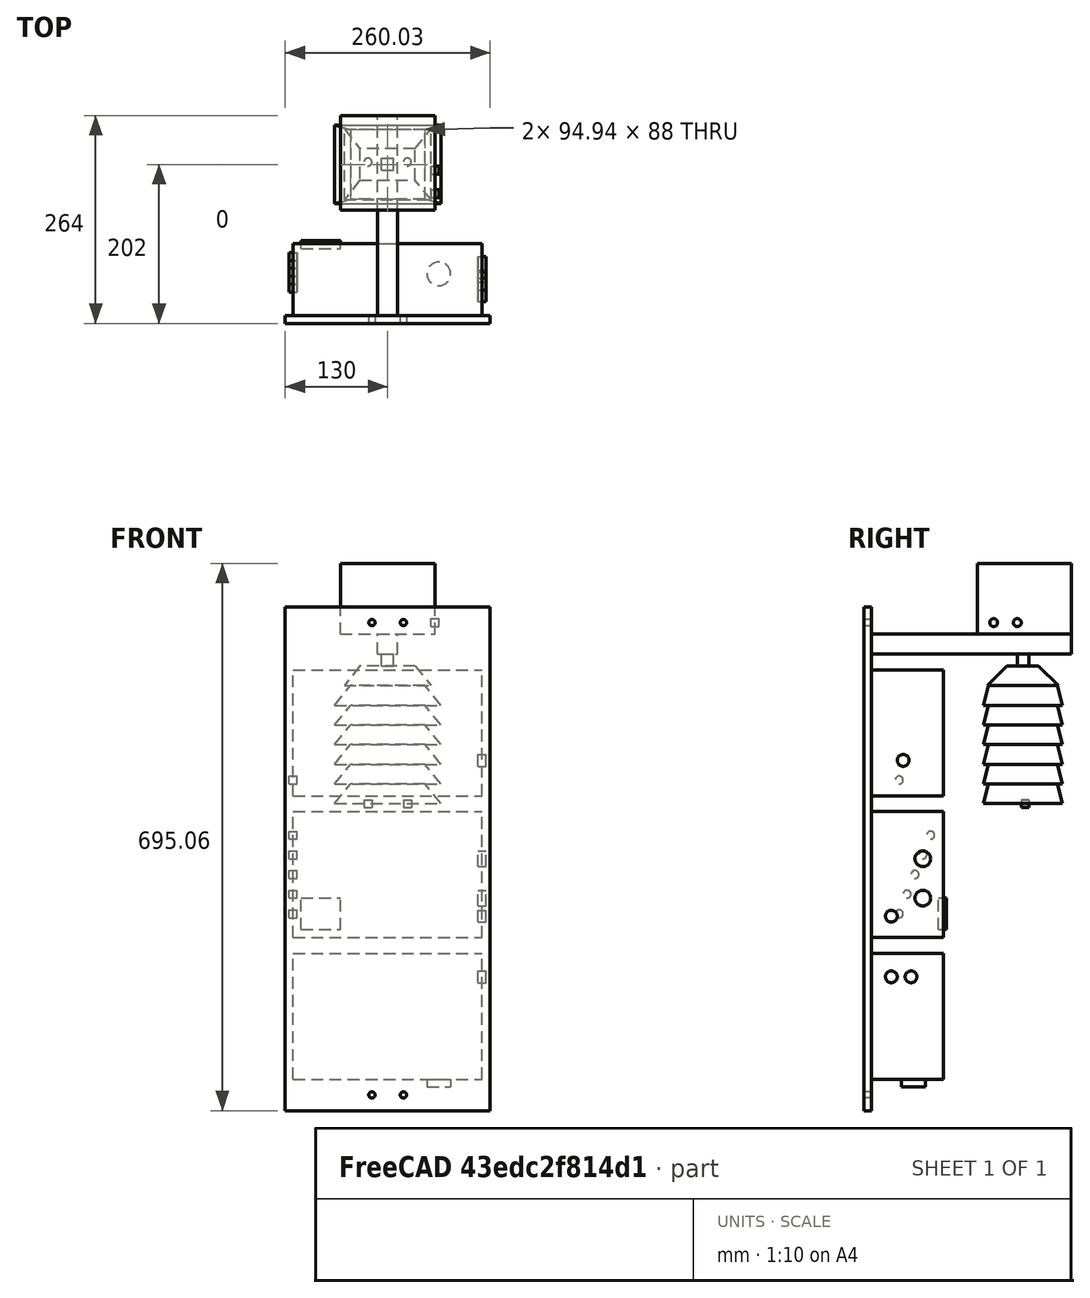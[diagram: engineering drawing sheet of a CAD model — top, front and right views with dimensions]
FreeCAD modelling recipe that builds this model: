
FCSTD DOCUMENT  (FreeCAD 0.17R13541 (Git))
Label: centralNode2019
License: All rights reserved
LicenseURL: http://en.wikipedia.org/wiki/All_rights_reserved
objects: Part::Box×38, Part::Cylinder×19, Part::Cut×17, Part::MultiCommon×10, Part::MultiFuse×3
note: 87 computed .brp shape members not serialized (recipe doc carries the construction recipe); baked Part::Feature solids carry a one-line shape summary decoded from their .brp

FEATURE [Part::Box] Box  label="Power Module "
  AttacherType = Attacher::AttachEngine3D
  Height = 160.02
  Length = 240.03
  Width = 91.44
FEATURE [Part::Box] Box001  label="Main Module"
  AttacherType = Attacher::AttachEngine3D
  Height = 160.02
  Length = 240.03
  Placement = pos=(0,0,180) rot=(0,0,1;0rad)
  Width = 91.44
FEATURE [Part::Box] Box002  label="Ozone Module"
  AttacherType = Attacher::AttachEngine3D
  Height = 160.02
  Length = 240.03
  Placement = pos=(0,0,360) rot=(0,0,1;0rad)
  Width = 91.44
FEATURE [Part::Box] Box003  label="Light Module"
  AttacherType = Attacher::AttachEngine3D
  Height = 89.66
  Length = 119.89
  Placement = pos=(60.05,134.1,565.4) rot=(0,0,1;0rad)
  Width = 119.89
FEATURE [Part::Box] Box005  label="Railing"
  AttacherType = Attacher::AttachEngine3D
  Height = 25.4
  Length = 25.4
  Placement = pos=(107.3,0,540) rot=(0,0,1;0rad)
  Width = 254
FEATURE [Part::Box] Box006  label="BackPanel"
  AttacherType = Attacher::AttachEngine3D
  Height = 640
  Length = 260.03
  Placement = pos=(-10,-10,-40) rot=(0,0,1;0rad)
  Width = 10
FEATURE [Part::Box] Box008  label="Cube001"
  AttacherType = Attacher::AttachEngine3D
  Height = 200
  Length = 200
  Placement = pos=(-22,-226,0) rot=(-1,0,0;0.235619rad)
  Width = 500
FEATURE [Part::Box] Box009  label="Acu1"
  AttacherType = Attacher::AttachEngine3D
  Height = 25
  Length = 135
  Placement = pos=(0,-226,0) rot=(0,0,1;0rad)
  Width = 100
FEATURE [Part::Box] Box010  label="Cube"
  AttacherType = Attacher::AttachEngine3D
  Height = 200
  Length = 20
  Placement = pos=(135,-236,0) rot=(0,-1,0;0.675442rad)
  Width = 500
FEATURE [Part::Box] Box011  label="Cube002"
  AttacherType = Attacher::AttachEngine3D
  Height = 500
  Length = 500
  Placement = pos=(0,-236,0) rot=(0,1,0;0.675442rad)
  Width = 500
FEATURE [Part::Cut] Cut
  Base = -> Box009
  Tool = -> Box010
FEATURE [Part::MultiCommon] Common
  Shapes = -> [Box011,Cut]
FEATURE [Part::MultiCommon] Common001
  Shapes = -> [Common,Box008]
FEATURE [Part::Box] Box012  label="Cube003"
  AttacherType = Attacher::AttachEngine3D
  Height = 88
  Length = 200
  Placement = pos=(-33,-126,0) rot=(1,0,0;0.235619rad)
  Width = 55
FEATURE [Part::Cut] Cut001  label="Enclosure Common000"
  Base = -> Common001
  Placement = pos=(52.5,368,475) rot=(0,0,1;0rad)
  Tool = -> Box012
FEATURE [Part::Box] Box013  label="Cube004"
  AttacherType = Attacher::AttachEngine3D
  Height = 25
  Length = 110
  Placement = pos=(311,-226,0) rot=(0,0,1;0rad)
  Width = 90
FEATURE [Part::Box] Box014  label="Cube005"
  AttacherType = Attacher::AttachEngine3D
  Height = 25
  Length = 110
  Placement = pos=(311,-226,0) rot=(1,0,0;0.785398rad)
  Width = 90
FEATURE [Part::Box] Box015  label="Cube006"
  AttacherType = Attacher::AttachEngine3D
  Height = 42
  Length = 110
  Placement = pos=(311,-136,0) rot=(1,0,0;0.785398rad)
  Width = 90
FEATURE [Part::Box] Box017  label="Cube008"
  AttacherType = Attacher::AttachEngine3D
  Height = 46
  Length = 110
  Placement = pos=(421,-226,0) rot=(0,-1,0;0.675442rad)
  Width = 120
FEATURE [Part::Cut] Cut002
  Base = -> Box013
  Tool = -> Box014
FEATURE [Part::Box] Box018  label="Cube009"
  AttacherType = Attacher::AttachEngine3D
  Height = 15
  Length = 15
  Placement = pos=(112.5,185,525) rot=(0,0,1;0rad)
  Width = 15
FEATURE [Part::Box] Box019  label="Acu002"
  AttacherType = Attacher::AttachEngine3D
  Height = 25
  Length = 135
  Placement = pos=(0,-226,0) rot=(0,0,1;0rad)
  Width = 100
FEATURE [Part::Box] Box020  label="Cube010"
  AttacherType = Attacher::AttachEngine3D
  Height = 200
  Length = 200
  Placement = pos=(-22,-226,0) rot=(-1,0,0;0.235619rad)
  Width = 500
FEATURE [Part::Box] Box021  label="Cube011"
  AttacherType = Attacher::AttachEngine3D
  Height = 500
  Length = 500
  Placement = pos=(0,-236,0) rot=(0,1,0;0.675442rad)
  Width = 500
FEATURE [Part::Box] Box022  label="Cube012"
  AttacherType = Attacher::AttachEngine3D
  Height = 200
  Length = 20
  Placement = pos=(135,-236,0) rot=(0,-1,0;0.675442rad)
  Width = 500
FEATURE [Part::Box] Box023  label="Cube013"
  AttacherType = Attacher::AttachEngine3D
  Height = 88
  Length = 200
  Placement = pos=(-33,-126,0) rot=(1,0,0;0.235619rad)
  Width = 55
FEATURE [Part::Cut] Cut007
  Base = -> Box019
  Tool = -> Box022
FEATURE [Part::MultiCommon] Common002
  Shapes = -> [Box021,Cut007]
FEATURE [Part::MultiCommon] Common003
  Shapes = -> [Common002,Box020]
FEATURE [Part::Cut] Cut006  label="Enclosure Common001"
  Base = -> Common003
  Placement = pos=(52.5,368,450) rot=(0,0,1;0rad)
  Tool = -> Box023
FEATURE [Part::Box] Box024  label="Acu003"
  AttacherType = Attacher::AttachEngine3D
  Height = 25
  Length = 135
  Placement = pos=(0,-226,0) rot=(0,0,1;0rad)
  Width = 100
FEATURE [Part::Box] Box025  label="Cube014"
  AttacherType = Attacher::AttachEngine3D
  Height = 200
  Length = 200
  Placement = pos=(-22,-226,0) rot=(-1,0,0;0.235619rad)
  Width = 500
FEATURE [Part::Box] Box026  label="Cube015"
  AttacherType = Attacher::AttachEngine3D
  Height = 88
  Length = 200
  Placement = pos=(-33,-126,0) rot=(1,0,0;0.235619rad)
  Width = 55
FEATURE [Part::Box] Box027  label="Cube016"
  AttacherType = Attacher::AttachEngine3D
  Height = 500
  Length = 500
  Placement = pos=(0,-236,0) rot=(0,1,0;0.675442rad)
  Width = 500
FEATURE [Part::Box] Box028  label="Cube017"
  AttacherType = Attacher::AttachEngine3D
  Height = 200
  Length = 20
  Placement = pos=(135,-236,0) rot=(0,-1,0;0.675442rad)
  Width = 500
FEATURE [Part::Cut] Cut008
  Base = -> Box024
  Tool = -> Box028
FEATURE [Part::MultiCommon] Common005
  Shapes = -> [Box027,Cut008]
FEATURE [Part::MultiCommon] Common004
  Shapes = -> [Common005,Box025]
FEATURE [Part::Cut] Cut009  label="Enclosure Common002"
  Base = -> Common004
  Placement = pos=(52.5,368,425) rot=(0,0,1;0rad)
  Tool = -> Box026
FEATURE [Part::Box] Box029  label="Acu004"
  AttacherType = Attacher::AttachEngine3D
  Height = 25
  Length = 135
  Placement = pos=(0,-226,0) rot=(0,0,1;0rad)
  Width = 100
FEATURE [Part::Box] Box030  label="Cube018"
  AttacherType = Attacher::AttachEngine3D
  Height = 200
  Length = 200
  Placement = pos=(-22,-226,0) rot=(-1,0,0;0.235619rad)
  Width = 500
FEATURE [Part::Box] Box031  label="Cube019"
  AttacherType = Attacher::AttachEngine3D
  Height = 88
  Length = 200
  Placement = pos=(-33,-126,0) rot=(1,0,0;0.235619rad)
  Width = 55
FEATURE [Part::Box] Box032  label="Cube020"
  AttacherType = Attacher::AttachEngine3D
  Height = 500
  Length = 500
  Placement = pos=(0,-236,0) rot=(0,1,0;0.675442rad)
  Width = 500
FEATURE [Part::Box] Box033  label="Cube021"
  AttacherType = Attacher::AttachEngine3D
  Height = 200
  Length = 20
  Placement = pos=(135,-236,0) rot=(0,-1,0;0.675442rad)
  Width = 500
FEATURE [Part::Cut] Cut010
  Base = -> Box029
  Tool = -> Box033
FEATURE [Part::MultiCommon] Common007
  Shapes = -> [Box032,Cut010]
FEATURE [Part::MultiCommon] Common006
  Shapes = -> [Common007,Box030]
FEATURE [Part::Cut] Cut011  label="Enclosure Common003"
  Base = -> Common006
  Placement = pos=(52.5,368,400) rot=(0,0,1;0rad)
  Tool = -> Box031
FEATURE [Part::Box] Box034  label="Acu005"
  AttacherType = Attacher::AttachEngine3D
  Height = 25
  Length = 135
  Placement = pos=(0,-226,0) rot=(0,0,1;0rad)
  Width = 100
FEATURE [Part::Box] Box035  label="Cube022"
  AttacherType = Attacher::AttachEngine3D
  Height = 200
  Length = 200
  Placement = pos=(-22,-226,0) rot=(-1,0,0;0.235619rad)
  Width = 500
FEATURE [Part::Box] Box036  label="Cube023"
  AttacherType = Attacher::AttachEngine3D
  Height = 88
  Length = 200
  Placement = pos=(-33,-126,0) rot=(1,0,0;0.235619rad)
  Width = 55
FEATURE [Part::Box] Box037  label="Cube024"
  AttacherType = Attacher::AttachEngine3D
  Height = 500
  Length = 500
  Placement = pos=(0,-236,0) rot=(0,1,0;0.675442rad)
  Width = 500
FEATURE [Part::Box] Box038  label="Cube025"
  AttacherType = Attacher::AttachEngine3D
  Height = 200
  Length = 20
  Placement = pos=(135,-236,0) rot=(0,-1,0;0.675442rad)
  Width = 500
FEATURE [Part::Cut] Cut012
  Base = -> Box034
  Tool = -> Box038
FEATURE [Part::MultiCommon] Common009
  Shapes = -> [Box037,Cut012]
FEATURE [Part::MultiCommon] Common008
  Shapes = -> [Common009,Box035]
FEATURE [Part::Cut] Cut013  label="Enclosure Common004"
  Base = -> Common008
  Placement = pos=(52.5,368,375) rot=(0,0,1;0rad)
  Tool = -> Box036
FEATURE [Part::Cut] Cut014  label="Enclosure Common005"
  Base = -> Common001
  Placement = pos=(52.5,368,350) rot=(0,0,1;0rad)
  Tool = -> Box012
FEATURE [Part::Cut] Cut003
  Base = -> Cut002
  Tool = -> Box015
FEATURE [Part::Box] Box016  label="Cube007"
  AttacherType = Attacher::AttachEngine3D
  Height = 25
  Length = 110
  Placement = pos=(311,-226,0) rot=(0,-1,0;0.912807rad)
  Width = 90
FEATURE [Part::Cut] Cut004
  Base = -> Cut003
  Tool = -> Box016
FEATURE [Part::Cut] Cut005  label="EnclousureTop"
  Base = -> Cut004
  Placement = pos=(-246,373,500) rot=(0,0,1;0rad)
  Tool = -> Box017
FEATURE [Part::Cylinder] Cylinder
  Angle = 360
  AttacherType = Attacher::AttachEngine3D
  Height = 10
  Placement = pos=(185,53,0) rot=(0,1,0;3.14159rad)
  Radius = 15
FEATURE [Part::Cylinder] Cylinder001  label="USB"
  Angle = 360
  AttacherType = Attacher::AttachEngine3D
  Height = 10
  Placement = pos=(235,65,230) rot=(0,1,0;1.5708rad)
  Radius = 10
FEATURE [Part::Cylinder] Cylinder002  label="HDMI"
  Angle = 360
  AttacherType = Attacher::AttachEngine3D
  Height = 10
  Placement = pos=(235,65,280) rot=(0,1,0;1.5708rad)
  Radius = 10
FEATURE [Part::Cylinder] Cylinder003  label="12V"
  Angle = 360
  AttacherType = Attacher::AttachEngine3D
  Height = 10
  Placement = pos=(235,50,130) rot=(0,1,0;1.5708rad)
  Radius = 7.5
FEATURE [Part::Cylinder] Cylinder004  label="5V"
  Angle = 360
  AttacherType = Attacher::AttachEngine3D
  Height = 10
  Placement = pos=(235,25,130) rot=(0,1,0;1.5708rad)
  Radius = 7.5
FEATURE [Part::Cylinder] Cylinder005  label="5V-2"
  Angle = 360
  AttacherType = Attacher::AttachEngine3D
  Height = 10
  Placement = pos=(235,25,207) rot=(0,1,0;1.5708rad)
  Radius = 7.5
FEATURE [Part::Cylinder] Cylinder006  label="12V-2"
  Angle = 360
  AttacherType = Attacher::AttachEngine3D
  Height = 10
  Placement = pos=(235,40,405) rot=(0,1,0;1.5708rad)
  Radius = 7.5
FEATURE [Part::Cylinder] Cylinder007  label="LightModuleUsb"
  Angle = 360
  AttacherType = Attacher::AttachEngine3D
  Height = 10
  Placement = pos=(-5,75,310) rot=(0,1,0;1.5708rad)
  Radius = 5
FEATURE [Part::Cylinder] Cylinder008  label="AirModuleUsb"
  Angle = 360
  AttacherType = Attacher::AttachEngine3D
  Height = 10
  Placement = pos=(-5,55,260) rot=(0,1,0;1.5708rad)
  Radius = 5
FEATURE [Part::Cylinder] Cylinder009  label="MicUsb"
  Angle = 360
  AttacherType = Attacher::AttachEngine3D
  Height = 10
  Placement = pos=(-5,45,235) rot=(0,1,0;1.5708rad)
  Radius = 5
FEATURE [Part::Cylinder] Cylinder010  label="OzoneUsb"
  Angle = 360
  AttacherType = Attacher::AttachEngine3D
  Height = 10
  Placement = pos=(-5,35,210) rot=(0,1,0;1.5708rad)
  Radius = 5
FEATURE [Part::Cylinder] Cylinder011  label="CameraUSB"
  Angle = 360
  AttacherType = Attacher::AttachEngine3D
  Height = 10
  Placement = pos=(-5,65,285) rot=(0,1,0;1.5708rad)
  Radius = 5
FEATURE [Part::Cylinder] Cylinder012  label="OzoneUsb-2"
  Angle = 360
  AttacherType = Attacher::AttachEngine3D
  Height = 10
  Placement = pos=(-5,35,380) rot=(0,1,0;1.5708rad)
  Radius = 5
FEATURE [Part::Cylinder] Cylinder013  label="LightModuleUsb-2"
  Angle = 360
  AttacherType = Attacher::AttachEngine3D
  Height = 10
  Placement = pos=(175,155,580) rot=(0,1,0;1.5708rad)
  Radius = 5
FEATURE [Part::Cylinder] Cylinder014  label="CameraUsb-2"
  Angle = 360
  AttacherType = Attacher::AttachEngine3D
  Height = 10
  Placement = pos=(175,185,580) rot=(0,1,0;1.5708rad)
  Radius = 5
FEATURE [Part::Cylinder] Cylinder015  label="MicUsb-2"
  Angle = 360
  AttacherType = Attacher::AttachEngine3D
  Height = 10
  Placement = pos=(145,195,355) rot=(0,1,0;3.14159rad)
  Radius = 5
FEATURE [Part::Cylinder] Cylinder016  label="AirUsb-2"
  Angle = 360
  AttacherType = Attacher::AttachEngine3D
  Height = 10
  Placement = pos=(95,195,355) rot=(0,1,0;3.14159rad)
  Radius = 5
FEATURE [Part::Cylinder] Cylinder017  label="CutOut"
  Angle = 360
  AttacherType = Attacher::AttachEngine3D
  Height = 10
  Placement = pos=(140,0,-20) rot=(1,0,0;1.5708rad)
  Radius = 4
FEATURE [Part::Cylinder] Cylinder018  label="CutOut001"
  Angle = 360
  AttacherType = Attacher::AttachEngine3D
  Height = 10
  Placement = pos=(100,0,-20) rot=(1,0,0;1.5708rad)
  Radius = 4
FEATURE [Part::MultiFuse] Fusion  label="Cutout1"
  Shapes = -> [Cylinder017,Cylinder018]
FEATURE [Part::MultiFuse] Fusion001
  Shapes = -> [Cut006,Cut009,Cut011,Cut013,Cut014,Cut001]
FEATURE [Part::MultiFuse] Fusion002  label="Cutout2"
  Placement = pos=(0,0,600) rot=(0,0,1;0rad)
  Shapes = -> [Cylinder017,Cylinder018]
FEATURE [Part::Cut] Cut015
  Base = -> Box006
  Tool = -> Fusion
FEATURE [Part::Box] Box039  label="Dispay"
  AttacherType = Attacher::AttachEngine3D
  Height = 40
  Length = 50
  Placement = pos=(10,85,190) rot=(0,0,1;0rad)
  Width = 10
FEATURE [Part::Cut] Cut016
  Base = -> Cut015
  Tool = -> Fusion002
